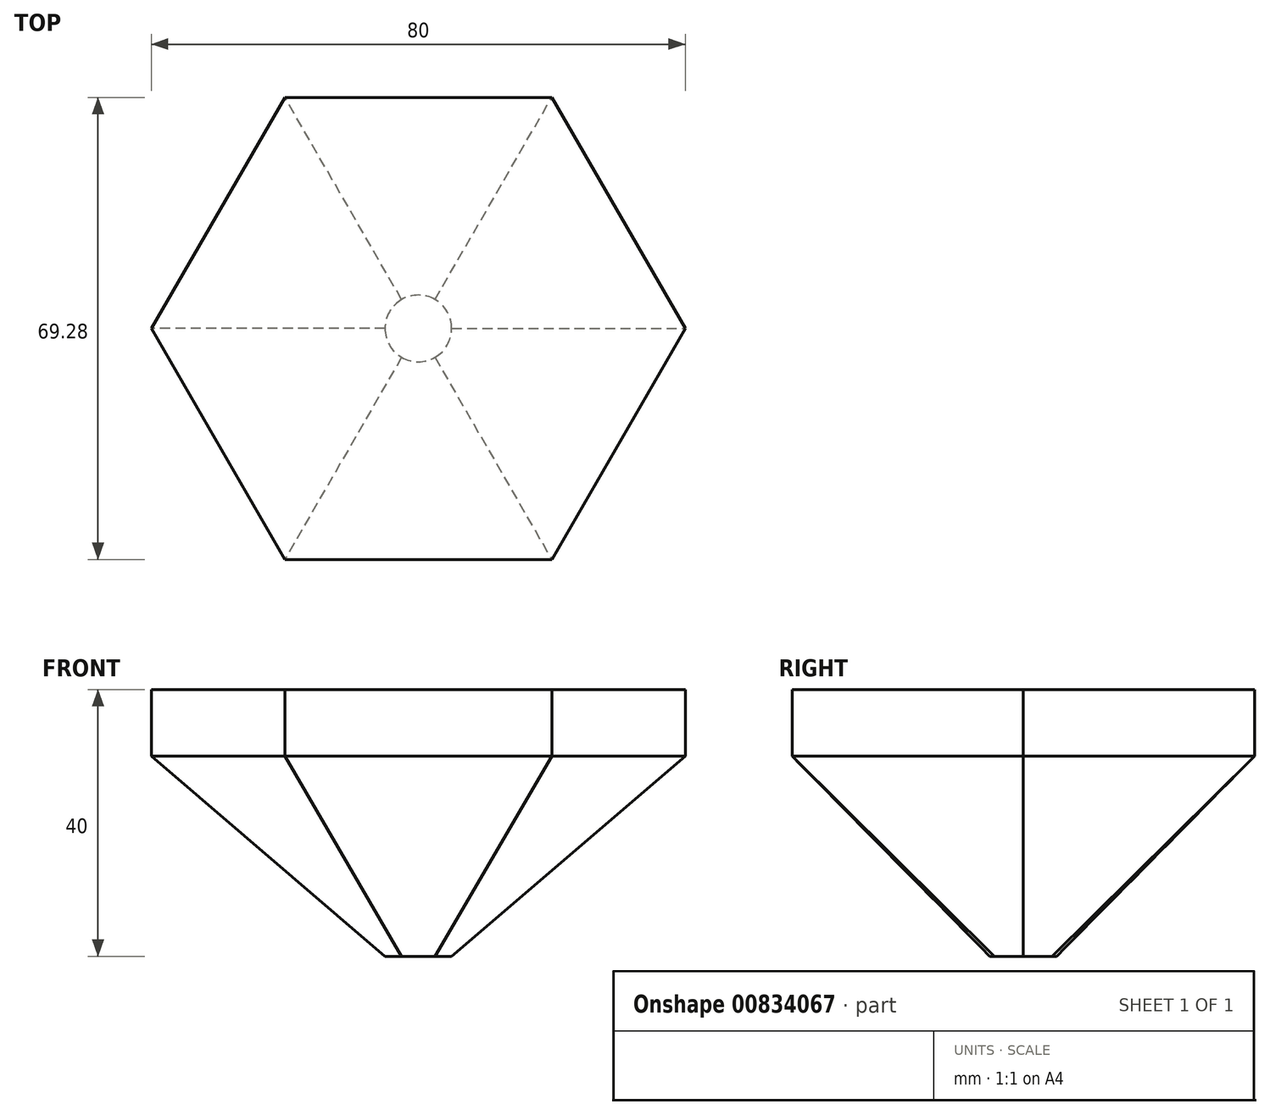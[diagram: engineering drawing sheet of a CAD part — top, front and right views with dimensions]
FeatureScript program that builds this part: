
annotation { "Feature Type Name" : "Feature", "Feature Type Description" : "" }
export const myFeature = defineFeature(function(context is Context, id is Id, definition is map)
    precondition{}
    {
        {
            var Q0;
            Q0=qCreatedBy(makeId("Top.planeOp"),FACE);
            var sketch = newSketch(context, id + "F0", { "sketchPlane" : qUnion([Q0])});
            skCircle(sketch, "E0.cCircle", {"center": v(0, 0) * mm, "radius": 40 * mm, "construction": true});
            skLineSegment(sketch, "E0.0", {"start": v(40, 0) * mm, "end": v(20, -34.64) * mm});
            skLineSegment(sketch, "E0.1", {"start": v(20, -34.64) * mm, "end": v(-20, -34.64) * mm});
            skLineSegment(sketch, "E0.2", {"start": v(-20, -34.64) * mm, "end": v(-40, 0) * mm});
            skLineSegment(sketch, "E0.3", {"start": v(-40, 0) * mm, "end": v(-20, 34.64) * mm});
            skLineSegment(sketch, "E0.4", {"start": v(-20, 34.64) * mm, "end": v(20, 34.64) * mm});
            skLineSegment(sketch, "E0.5", {"start": v(20, 34.64) * mm, "end": v(40, 0) * mm});
            skSolve(sketch);
        }
        {
            var Q0;
            Q0 = qSketchRegion(id + "F0", true);
            extrude(context, id + "F1", {"entities" : qUnion([Q0]), "depth" : 40 * mm, "offsetDistance" : 25 * mm});
        }
        {
            var Q0;
            Q0=makeQuery(id+"F1.opExtrude","CAP_FACE",FACE,{"disambiguationData":[OSD([sQuery(id+"F0.wireOp",EDGE,"E0.0"),sQuery(id+"F0.wireOp",EDGE,"E0.1"),sQuery(id+"F0.wireOp",EDGE,"E0.2"),sQuery(id+"F0.wireOp",EDGE,"E0.3"),sQuery(id+"F0.wireOp",EDGE,"E0.4"),sQuery(id+"F0.wireOp",EDGE,"E0.5")])],"isStart":true});
            var sketch = newSketch(context, id + "F2", { "sketchPlane" : qUnion([Q0])});
            skLineSegment(sketch, "E1.0.0", {"start": v(20, -34.64) * mm, "end": v(40, 0) * mm});
            skLineSegment(sketch, "E1.0.1", {"start": v(40, 0) * mm, "end": v(20, 34.64) * mm});
            skLineSegment(sketch, "E1.0.2", {"start": v(20, 34.64) * mm, "end": v(-20, 34.64) * mm});
            skLineSegment(sketch, "E1.0.3", {"start": v(-20, 34.64) * mm, "end": v(-40, 0) * mm});
            skLineSegment(sketch, "E1.0.4", {"start": v(-40, 0) * mm, "end": v(-20, -34.64) * mm});
            skLineSegment(sketch, "E1.0.5", {"start": v(-20, -34.64) * mm, "end": v(20, -34.64) * mm});
            skSolve(sketch);
        }
        {
            var Q0;
            Q0 = qSketchRegion(id + "F2", true);
            extrude(context, id + "F3", {"entities" : qUnion([Q0]), "operationType" : NewBodyOperationType.REMOVE, "oppositeDirection" : true, "depth" : 30 * mm, "offsetDistance" : 25 * mm});
        }
        {
            var Q0;
            Q0=makeQuery(id+"F3.boolean.opBoolean","COPY",FACE,{"derivedFrom":makeQuery(id+"F3.opExtrude","CAP_FACE",FACE,{"disambiguationData":[OSD([sQuery(id+"F2.wireOp",EDGE,"E1.0.0"),sQuery(id+"F2.wireOp",EDGE,"E1.0.1"),sQuery(id+"F2.wireOp",EDGE,"E1.0.2"),sQuery(id+"F2.wireOp",EDGE,"E1.0.3"),sQuery(id+"F2.wireOp",EDGE,"E1.0.4"),sQuery(id+"F2.wireOp",EDGE,"E1.0.5")])],"isStart":false})});
            var sketch = newSketch(context, id + "F4", { "sketchPlane" : qUnion([Q0])});
            skLineSegment(sketch, "E2.0.0", {"start": v(-20, -34.64) * mm, "end": v(20, -34.64) * mm});
            skLineSegment(sketch, "E2.0.1", {"start": v(20, -34.64) * mm, "end": v(40, 0) * mm});
            skLineSegment(sketch, "E2.0.2", {"start": v(40, 0) * mm, "end": v(20, 34.64) * mm});
            skLineSegment(sketch, "E2.0.3", {"start": v(20, 34.64) * mm, "end": v(-20, 34.64) * mm});
            skLineSegment(sketch, "E2.0.4", {"start": v(-20, 34.64) * mm, "end": v(-40, 0) * mm});
            skLineSegment(sketch, "E2.0.5", {"start": v(-40, 0) * mm, "end": v(-20, -34.64) * mm});
            skSolve(sketch);
        }
        {
            var Q0;
            Q0=qCreatedBy(makeId("Top.planeOp"),FACE);
            var sketch = newSketch(context, id + "F5", { "sketchPlane" : qUnion([Q0])});
            skCircle(sketch, "E3", {"center": v(0, 0) * mm, "radius": 5 * mm});
            skSolve(sketch);
        }
        {
            var Q1;
            Q1 = qSketchRegion(id + "F5", true);
            var Q2;
            Q2 = qSketchRegion(id + "F4", true);
            loft(context, id + "F6", {"operationType" : NewBodyOperationType.ADD, "sheetProfilesArray" : [{ "sheetProfileEntities" : qUnion([Q1]) }, { "sheetProfileEntities" : qUnion([Q2]) }]});
        }
    });
